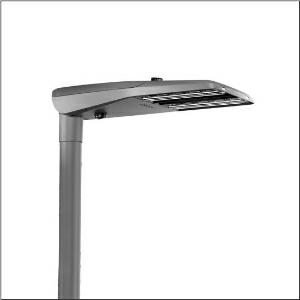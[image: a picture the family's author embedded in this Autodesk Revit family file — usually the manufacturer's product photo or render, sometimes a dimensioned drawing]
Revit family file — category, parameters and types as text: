
# Revit family: streetlight_sl_11_iq_midi___st1_2a_5xc3a21y08me_d9a7
name_source: partatom
category: Lighting Fixtures
units: mm (PartAtom-declared; Revit-internal decimal feet)

## family parameters
Cut with Voids When Loaded = No
Host = Face
Light Source = No
Part Type = Normal
Room Calculation Point = No
Round Connector Dimension = Use Diameter
Shared = No

## types (1)
- --- (1 x LED, 14840 lm, 122.8 W, 2200K)
    Apparent Load = 123 VA
    CIE Flux Codes = 32 70 96 100 100
    Color Rendering = 70
    Color Temperature = 2200K
    Default Elevation = 1800 mm
    Description = Streetlight SL 11 iQ midi, mast luminaire, primary light control with 3 zone facetted reflector, of plastic, silver coated, highly specular, primary optical cover: cover, of PMMA, transparent, light distribution: ST1.2a, light emission: direct distribution, primary light characteristic: asymmetric, installation type: post-top, side-entry, lamps: LED, High Power LED, rated values: 14.840lm | 122,8W | 120,8lm/W (begin service life); end service life: 14.840lm | 130,2W; at 50% lumin. flux: 7.420lm | 56,1W | 132,3lm/W, colour temperature: 2200K, colour rendering: CRI > 70, light colour: 722, light setting 1 begin service life: 100% | 14.840lm | 122,8W | 120,8lm/W | 2.200K, light setting 1 end service life: 130,2W, further light settings possible, control: pre-setting: logarithmic dimming characteristic, Street-Remote, Auto-Match, Temp-Guard, Lumen-Switch, Night-Set, Smart-Wire, Light-Fading, Desk-Remote (wireless, voltage-free reading and setting of iQ features in the workshop via application-optimized NFC function/RFID function), optimised constant luminous flux control (CLO 2.0), with cable H07RN-F 3x 1.5mm², mains connection: 230..240V, AC, 50/60Hz, connection cable pre-assembled, cable length: 12,5m, luminaire housing, of diecast aluminium, powder-coated, SITECO metallic grey (DB 702S), please order mast flange separately, inclination adjustable without tools: 0°, 5°, 10°, 15° (post-top) | 0°, -5°, -10°, -15° (side-entry), sealing non-destructively replaceable, multi-level sealing system, length: 780mm, width: 376mm, height: 118mm, mast flange for spigot size: 42mm (side-entry): 5XC10008XM4, 60/48mm (side-entry/post-top): 5XC10108XM2, 76/60mm (side-entry/post-top): 5XC10108XM1, equipment: Power, Smart Interface below and above, protection rating (complete): IP66, insulation class (complete): insulation class II (safety insulation), certification: CE, ENEC, ENEC+, VDE, UKCA, impact resistance: IK10, permissible operating ambient temperature for outdoor applications: -25..+50°C, standard-compliant lighting for roads and squares, Environmental Product Declaration (EPD) tested and certified by an independent institute, packaging unit: 1 piece

Light Distribution: ST1.2a
    Height = 118 mm
    Lamp = 1 x LED
    Lamp Light Flux = 14840 lm
    Lamp Power = 122.8 W
    Lamp count = 1
    Length = 780 mm
    Luminous efficacy = 121 lm/W
    Manufacturer = Siteco
    ModVariant = No
    Model = 5XC3A21Y08ME
    Number of Poles = 1
    OnlyDefault = Yes
    Power Factor = 1
    Product Name = Streetlight SL 11 iQ midi | ST1.2a
    Product group = mast luminaire | pylon top
    ProductGroupID = 6100
    Protection Class = Protection class II
    Protection Degree = IP 66
    RLX_Detail_Level = 1
    RLX_Emergency_Light_Flux = 0 lm
    RLX_Emergency_Type = 0
    RLX_Emergency_Type_DB = No
    RlxData = <blob elided: 69913 chars, md5=fe93529b>
    Socket = socket
    Standby Power = 0 W
    System Light Flux = 14840 lm
    System Power = 123 W
    Type Comments = factory setting: luminous flux: 100 % | dim-lin: 254 | 553 mA
    Type Image = l_1004429.jpg
    URL = http://relux.com
    VarID = @adj_129557
    Voltage = 0 V
    Weight = 0.00 kg
    Width = 376 mm

## geometry (parser evidence)
native form markers: Blend x4, Sweep x9
no freeform markers — native parametric forms only
